# Revit family: Aquatica Gamma-515 Freestanding Outdoor Shower
name_source: partatom
category: Plumbing Fixtures
revit_build: Autodesk Revit 2018 (Build: 20170223_1515(x64)
units: mm (PartAtom-declared; Revit-internal decimal feet)

## family parameters
Always vertical = No
Cut with Voids When Loaded = No
OmniClass Number = 23.45.05.14.21.11
OmniClass Title = Bath/Shower Units
Part Type = Normal
Room Calculation Point = No
Round Connector Dimension = Use Radius
Shared = No
Work Plane-Based = No

## types (1)
- Gamma-515
    Assembly required = Yes
    Cold_Water_Supply_Radius = 1/2"
    Description = Aquatica’s elegant, new, slimline stainless Gamma-515 freestanding outdoor cold water shower features both a self-closing tap and a self-closing foot washer jet for a quick and easy rinse-down after a busy time at the beach, boating, gardening, sport or round the pool.
    Faucet height to aerator (cm) = 210
    Faucet spout height (cm) = 221.8
    Faucet spout reach (cm) = 40
    Hot_Water_Supply_Radius = 1/2"
    Manufacturer = Aquatica
    Model = Gamma
    Number of boxes = 1
    Product Exterior Material = Stainless Steel AISI 317
    Product Material = Stainless Steel 316L
    Warranty = 5 Year Limited Warranty

## geometry (parser evidence)
native form markers: Sweep x29
no freeform markers — native parametric forms only
